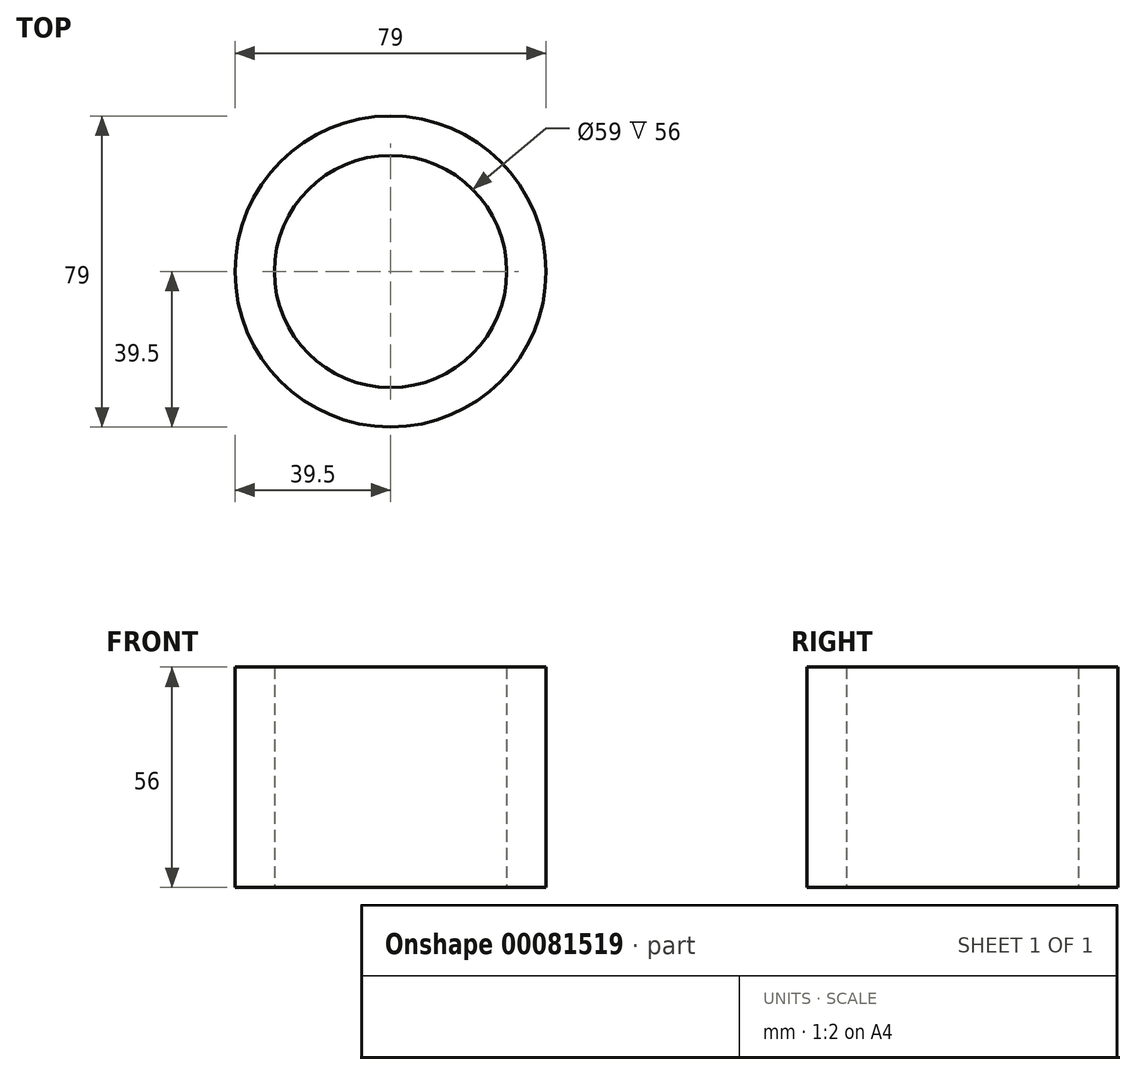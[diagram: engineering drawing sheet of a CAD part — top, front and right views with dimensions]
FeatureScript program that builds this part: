
annotation { "Feature Type Name" : "Feature", "Feature Type Description" : "" }
export const myFeature = defineFeature(function(context is Context, id is Id, definition is map)
    precondition{}
    {
        {
            var Q0;
            Q0=qCreatedBy(makeId("Top.planeOp"),FACE);
            var sketch = newSketch(context, id + "F0", { "sketchPlane" : qUnion([Q0])});
            skCircle(sketch, "E0", {"center": v(0, 0) * mm, "radius": 39.5 * mm});
            skCircle(sketch, "E1", {"center": v(0, 0) * mm, "radius": 29.5 * mm});
            skSolve(sketch);
        }
        {
            var Q0;
            Q0 = qSketchRegion(id + "F0", true);
            extrude(context, id + "F1", {"entities" : qUnion([Q0]), "depth" : 56 * mm});
        }
    });
